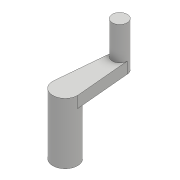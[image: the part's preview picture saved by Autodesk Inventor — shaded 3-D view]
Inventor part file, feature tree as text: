
AUTODESK INVENTOR PART (.ipt)
format: ipt  version: 2017 (Build 210142000, 142)  size: 90,112 bytes
history: native  units: mm
features: extrude x3, sketch x2
ambient origin geometry x8: Origin, YZ Plane, XZ Plane, XY Plane, X Axis, Y Axis, Z Axis, Center Point
bodies: Solid1 (feature_tree)
feature tree (5):
  extrude  "Extrusion1"  Depth=50.0mm TaperAngle=0.0deg
  sketch  "Sketch2"  dims[d3=15.0mm d4=11.5mm d5=0.0mm d6=45.0mm d7=0.0mm]
  extrude  "Extrusion2"  Depth=11.5mm TaperAngle=0.0deg
  extrude  "Extrusion3"  Depth=45.0mm TaperAngle=0.0deg
  sketch  "Sketch1"  dims[d0=25.0mm d1=50.0mm d2=0.0mm]
